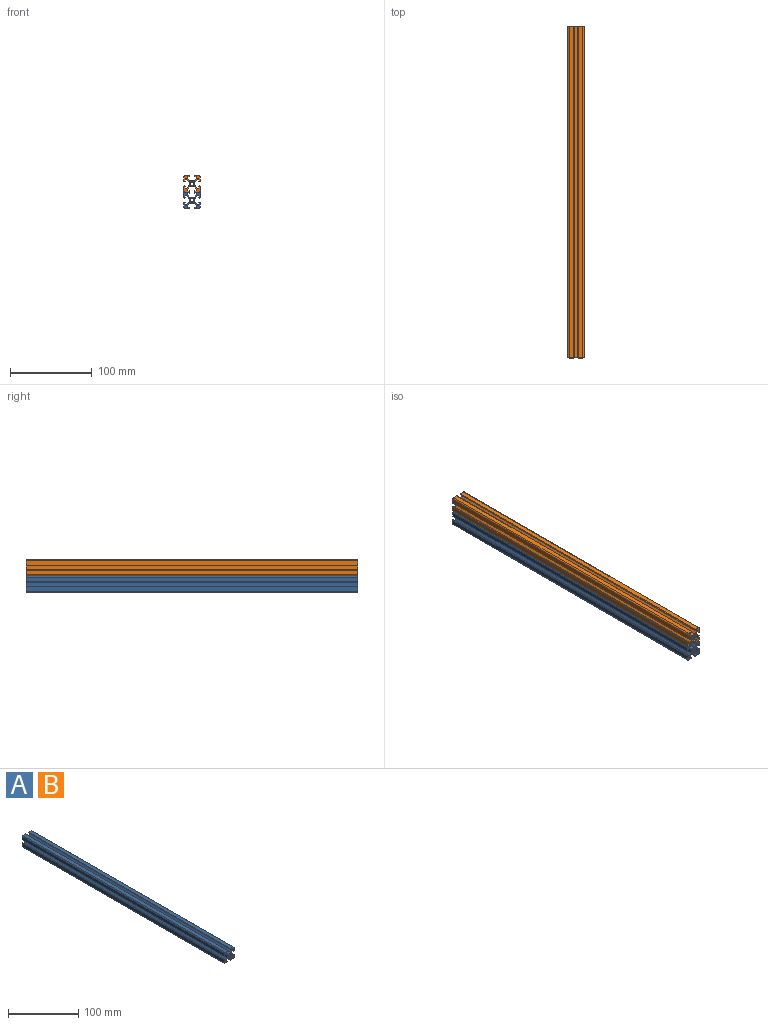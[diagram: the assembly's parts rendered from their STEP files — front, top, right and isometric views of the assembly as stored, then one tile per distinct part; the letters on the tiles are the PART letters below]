
ASSEMBLY  parts=2 mates=1
PART A: 106 faces, bbox 20x406.4x20 mm
  f0: cylinder r=2.11mm len=406.4mm, axis (0,1,0), area 670.5mm2, adj f1,f15,f16,f17
  f1: cylinder r=0.79mm len=406.4mm, axis (0,1,0), area 672.7mm2, adj f0,f2,f16,f17
  f2: plane 406.4x0.18mm, normal (0.71,0,0.71), area 103.2mm2, adj f1,f3,f16,f17
  f3: cylinder r=0.79mm len=406.4mm, axis (0,1,0), area 672.7mm2, adj f2,f4,f16,f17
  f4: cylinder r=2.11mm len=406.4mm, axis (0,1,0), area 670.5mm2, adj f3,f5,f16,f17
  f5: cylinder r=0.79mm len=406.4mm, axis (0,1,0), area 672.7mm2, adj f4,f6,f16,f17
  f6: plane 406.4x0.18mm, normal (-0.71,0,0.71), area 103.2mm2, adj f5,f7,f16,f17
  f7: cylinder r=0.79mm len=406.4mm, axis (0,1,0), area 672.7mm2, adj f6,f8,f16,f17
  f8: cylinder r=2.11mm len=406.4mm, axis (0,1,0), area 670.5mm2, adj f7,f9,f16,f17
  f9: cylinder r=0.79mm len=406.4mm, axis (0,1,0), area 672.7mm2, adj f8,f10,f16,f17
  f10: plane 406.4x0.18mm, normal (-0.71,0,-0.71), area 103.2mm2, adj f9,f11,f16,f17
  f11: cylinder r=0.79mm len=406.4mm, axis (0,1,0), area 672.7mm2, adj f10,f12,f16,f17
  f12: cylinder r=2.11mm len=406.4mm, axis (0,1,0), area 670.5mm2, adj f11,f13,f16,f17
  f13: cylinder r=0.79mm len=406.4mm, axis (0,1,0), area 672.7mm2, adj f12,f14,f16,f17
  f14: plane 406.4x0.18mm, normal (0.71,0,-0.71), area 103.2mm2, adj f13,f15,f16,f17
  f15: cylinder r=0.79mm len=406.4mm, axis (0,1,0), area 672.7mm2, adj f0,f14,f16,f17
  f16: plane 20x20mm, normal (0,-1,0), area 159.4mm2, adj f0,f1,f2,f3,f4,f5,f6,f7
  f17: plane 20x20mm, normal (0,1,0), area 159.4mm2, adj f0,f1,f2,f3,f4,f5,f6,f7
  f18: cylinder r=0.51mm len=406.4mm, axis (0,1,0), area 323.5mm2, adj f16,f17,f19,f105
  f19: plane 406.4x0.73mm, normal (-1,0,0), area 295mm2, adj f16,f17,f18,f20
  f20: cylinder r=0.51mm len=406.4mm, axis (0,1,0), area 162.1mm2, adj f16,f17,f19,f21
  f21: plane 406.4x3.1mm, normal (-0.71,0,-0.71), area 1783.5mm2, adj f16,f17,f20,f22
  f22: cylinder r=0.51mm len=406.4mm, axis (0,1,0), area 162.1mm2, adj f16,f17,f21,f23
  f23: plane 406.4x4.77mm, normal (0,0,-1), area 1937.6mm2, adj f16,f17,f22,f24
  f24: cylinder r=0.51mm len=406.4mm, axis (0,1,0), area 162.1mm2, adj f16,f17,f23,f25
  f25: plane 406.4x3.1mm, normal (0.71,0,-0.71), area 1783.5mm2, adj f16,f17,f24,f26
  f26: cylinder r=0.51mm len=406.4mm, axis (0,1,0), area 162.1mm2, adj f16,f17,f25,f27
  f27: plane 406.4x0.73mm, normal (1,0,0), area 295mm2, adj f16,f17,f26,f28
  f28: cylinder r=0.51mm len=406.4mm, axis (0,1,0), area 323.5mm2, adj f16,f17,f27,f29
  f29: plane 406.4x2.35mm, normal (0,0,1), area 954.6mm2, adj f16,f17,f28,f30
  f30: cylinder r=0.51mm len=406.4mm, axis (0,1,0), area 323.5mm2, adj f16,f17,f29,f31
  f31: plane 406.4x0.48mm, normal (1,0,0), area 196.7mm2, adj f16,f17,f30,f32
  f32: cylinder r=0.51mm len=406.4mm, axis (0,1,0), area 323.5mm2, adj f16,f17,f31,f33
  f33: plane 406.4x5.36mm, normal (0,0,-1), area 2179.1mm2, adj f16,f17,f32,f34
  f34: cylinder r=1.51mm len=406.4mm, axis (0,1,0), area 955mm2, adj f16,f17,f33,f35
  f35: plane 406.4x5.36mm, normal (-1,0,0), area 2179.1mm2, adj f16,f17,f34,f36
  f36: cylinder r=0.51mm len=406.4mm, axis (0,1,0), area 323.5mm2, adj f16,f17,f35,f37
  f37: plane 406.4x0.48mm, normal (0,0,1), area 196.7mm2, adj f16,f17,f36,f38
  f38: cylinder r=0.51mm len=406.4mm, axis (0,1,0), area 323.5mm2, adj f16,f17,f37,f39
  f39: plane 406.4x2.35mm, normal (1,0,0), area 954.6mm2, adj f16,f17,f38,f40
  f40: cylinder r=0.51mm len=406.4mm, axis (0,1,0), area 323.5mm2, adj f16,f17,f39,f41
  f41: plane 406.4x0.73mm, normal (0,0,1), area 295mm2, adj f16,f17,f40,f42
  f42: cylinder r=0.51mm len=406.4mm, axis (0,1,0), area 162.1mm2, adj f16,f17,f41,f43
  f43: plane 406.4x3.1mm, normal (-0.71,0,0.71), area 1783.5mm2, adj f16,f17,f42,f44
  f44: cylinder r=0.51mm len=406.4mm, axis (0,1,0), area 162.1mm2, adj f16,f17,f43,f45
  f45: plane 406.4x4.77mm, normal (-1,0,0), area 1937.6mm2, adj f16,f17,f44,f46
  f46: cylinder r=0.51mm len=406.4mm, axis (0,1,0), area 162.1mm2, adj f16,f17,f45,f47
  f47: plane 406.4x3.1mm, normal (-0.71,0,-0.71), area 1783.5mm2, adj f16,f17,f46,f48
  f48: cylinder r=0.51mm len=406.4mm, axis (0,1,0), area 162.1mm2, adj f16,f17,f47,f49
  f49: plane 406.4x0.73mm, normal (0,0,-1), area 295mm2, adj f16,f17,f48,f50
  f50: cylinder r=0.51mm len=406.4mm, axis (0,1,0), area 323.5mm2, adj f16,f17,f49,f51
  f51: plane 406.4x2.35mm, normal (1,0,0), area 954.6mm2, adj f16,f17,f50,f52
  f52: cylinder r=0.51mm len=406.4mm, axis (0,1,0), area 323.5mm2, adj f16,f17,f51,f53
  f53: plane 406.4x0.48mm, normal (0,0,-1), area 196.7mm2, adj f16,f17,f52,f54
  f54: cylinder r=0.51mm len=406.4mm, axis (0,1,0), area 323.5mm2, adj f16,f17,f53,f55
  f55: plane 406.4x5.36mm, normal (-1,0,0), area 2179.1mm2, adj f16,f17,f54,f56
  f56: cylinder r=1.51mm len=406.4mm, axis (0,1,0), area 955mm2, adj f16,f17,f55,f57
  f57: plane 406.4x5.36mm, normal (0,0,1), area 2179.1mm2, adj f16,f17,f56,f58
  f58: cylinder r=0.51mm len=406.4mm, axis (0,1,0), area 323.5mm2, adj f16,f17,f57,f59
  f59: plane 406.4x0.48mm, normal (1,0,0), area 196.7mm2, adj f16,f17,f58,f60
  f60: cylinder r=0.51mm len=406.4mm, axis (0,1,0), area 323.5mm2, adj f16,f17,f59,f61
  f61: plane 406.4x2.35mm, normal (0,0,-1), area 954.6mm2, adj f16,f17,f60,f62
  f62: cylinder r=0.51mm len=406.4mm, axis (0,1,0), area 323.5mm2, adj f16,f17,f61,f63
  f63: plane 406.4x0.73mm, normal (1,0,0), area 295mm2, adj f16,f17,f62,f64
  f64: cylinder r=0.51mm len=406.4mm, axis (0,1,0), area 162.1mm2, adj f16,f17,f63,f65
  f65: plane 406.4x3.1mm, normal (0.71,0,0.71), area 1783.5mm2, adj f16,f17,f64,f66
  f66: cylinder r=0.51mm len=406.4mm, axis (0,1,0), area 162.1mm2, adj f16,f17,f65,f67
  f67: plane 406.4x4.77mm, normal (0,0,1), area 1937.6mm2, adj f16,f17,f66,f68
  f68: cylinder r=0.51mm len=406.4mm, axis (0,1,0), area 162.1mm2, adj f16,f17,f67,f69
  f69: plane 406.4x3.1mm, normal (-0.71,0,0.71), area 1783.5mm2, adj f16,f17,f68,f70
  f70: cylinder r=0.51mm len=406.4mm, axis (0,1,0), area 162.1mm2, adj f16,f17,f69,f71
  f71: plane 406.4x0.73mm, normal (-1,0,0), area 295mm2, adj f16,f17,f70,f72
  f72: cylinder r=0.51mm len=406.4mm, axis (0,1,0), area 323.5mm2, adj f16,f17,f71,f73
  f73: plane 406.4x2.35mm, normal (0,0,-1), area 954.6mm2, adj f16,f17,f72,f74
  f74: cylinder r=0.51mm len=406.4mm, axis (0,1,0), area 323.5mm2, adj f16,f17,f73,f75
  f75: plane 406.4x0.48mm, normal (-1,0,0), area 196.7mm2, adj f16,f17,f74,f76
  f76: cylinder r=0.51mm len=406.4mm, axis (0,1,0), area 323.5mm2, adj f16,f17,f75,f77
  f77: plane 406.4x5.36mm, normal (0,0,1), area 2179.1mm2, adj f16,f17,f76,f78
  f78: cylinder r=1.51mm len=406.4mm, axis (0,1,0), area 955mm2, adj f16,f17,f77,f79
  f79: plane 406.4x5.36mm, normal (1,0,0), area 2179.1mm2, adj f16,f17,f78,f80
  f80: cylinder r=0.51mm len=406.4mm, axis (0,1,0), area 323.5mm2, adj f16,f17,f79,f81
  f81: plane 406.4x0.48mm, normal (0,0,-1), area 196.7mm2, adj f16,f17,f80,f82
  f82: cylinder r=0.51mm len=406.4mm, axis (0,1,0), area 323.5mm2, adj f16,f17,f81,f83
  f83: plane 406.4x2.35mm, normal (-1,0,0), area 954.6mm2, adj f16,f17,f82,f84
  f84: cylinder r=0.51mm len=406.4mm, axis (0,1,0), area 323.5mm2, adj f16,f17,f83,f85
  f85: plane 406.4x0.73mm, normal (0,0,-1), area 295mm2, adj f16,f17,f84,f86
  f86: cylinder r=0.51mm len=406.4mm, axis (0,1,0), area 162.1mm2, adj f16,f17,f85,f87
  f87: plane 406.4x3.1mm, normal (0.71,0,-0.71), area 1783.5mm2, adj f16,f17,f86,f88
  f88: cylinder r=0.51mm len=406.4mm, axis (0,1,0), area 162.1mm2, adj f16,f17,f87,f89
  f89: plane 406.4x4.77mm, normal (1,0,0), area 1937.6mm2, adj f16,f17,f88,f90
  f90: cylinder r=0.51mm len=406.4mm, axis (0,1,0), area 162.1mm2, adj f16,f17,f89,f91
  f91: plane 406.4x3.1mm, normal (0.71,0,0.71), area 1783.5mm2, adj f16,f17,f90,f92
  f92: cylinder r=0.51mm len=406.4mm, axis (0,1,0), area 162.1mm2, adj f16,f17,f91,f93
  f93: plane 406.4x0.73mm, normal (0,0,1), area 295mm2, adj f16,f17,f92,f94
  f94: cylinder r=0.51mm len=406.4mm, axis (0,1,0), area 323.5mm2, adj f16,f17,f93,f95
  f95: plane 406.4x2.35mm, normal (-1,0,0), area 954.6mm2, adj f16,f17,f94,f96
  f96: cylinder r=0.51mm len=406.4mm, axis (0,1,0), area 323.5mm2, adj f16,f17,f95,f97
  f97: plane 406.4x0.48mm, normal (0,0,1), area 196.7mm2, adj f16,f17,f96,f98
  f98: cylinder r=0.51mm len=406.4mm, axis (0,1,0), area 323.5mm2, adj f16,f17,f97,f99
  f99: plane 406.4x5.36mm, normal (1,0,0), area 2179.1mm2, adj f16,f17,f98,f100
  f100: cylinder r=1.51mm len=406.4mm, axis (0,1,0), area 955mm2, adj f16,f17,f99,f101
  f101: plane 406.4x5.36mm, normal (0,0,-1), area 2179.1mm2, adj f16,f17,f100,f102
  f102: cylinder r=0.51mm len=406.4mm, axis (0,1,0), area 323.5mm2, adj f16,f17,f101,f103
  f103: plane 406.4x0.48mm, normal (-1,0,0), area 196.7mm2, adj f16,f17,f102,f104
  f104: cylinder r=0.51mm len=406.4mm, axis (0,1,0), area 323.5mm2, adj f16,f17,f103,f105
  f105: plane 406.4x2.35mm, normal (0,0,1), area 954.6mm2, adj f16,f17,f18,f104
PART B: same geometry as A
PLACE A t=(10.32,0.25,-8.56)mm
PLACE B t=(10.32,0.25,11.44)mm
MATE fastened B.f16 <-> A.f16  axis (0,-1,0) through (18.82,-202.95,1.44)mm
